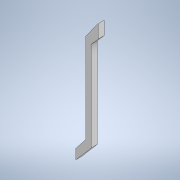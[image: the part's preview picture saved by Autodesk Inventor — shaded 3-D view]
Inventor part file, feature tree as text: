
AUTODESK INVENTOR PART (.ipt)
format: ipt  version: 2021 (Build 250183000, 183)  size: 105,472 bytes
history: native  units: mm
features: extrude x1, sketch x1
ambient origin geometry x8: Origin, YZ Plane, XZ Plane, XY Plane, X Axis, Y Axis, Z Axis, Center Point
bodies: Solide1 (feature_tree)
feature tree (2):
  extrude  "Extrusion1"  Depth=135.0mm
  sketch  "Esquisse1"
